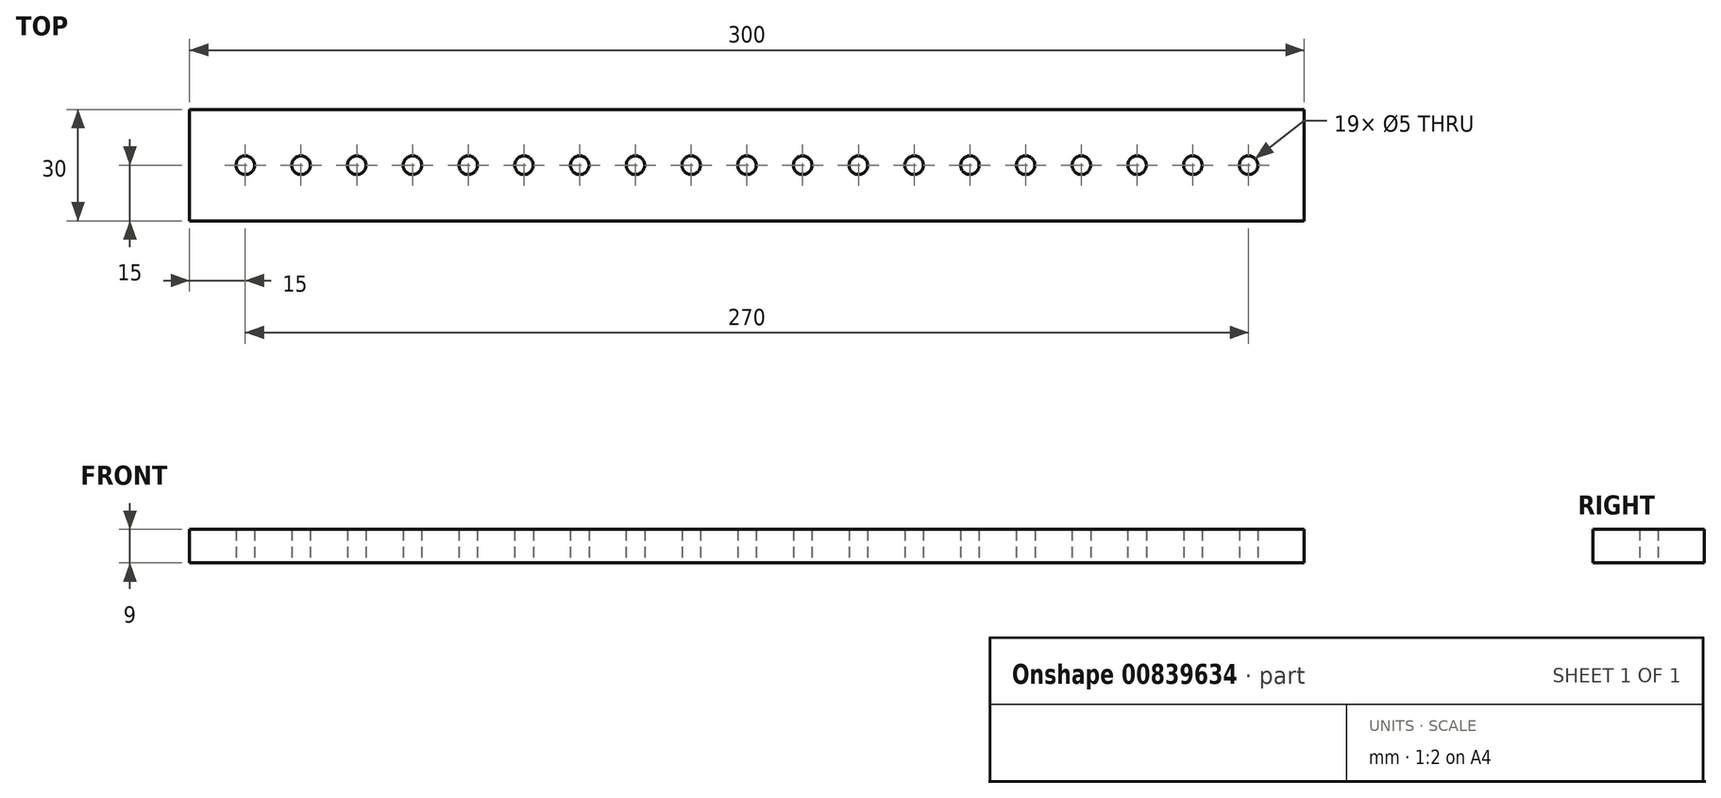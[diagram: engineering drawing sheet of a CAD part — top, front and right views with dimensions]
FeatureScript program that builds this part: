
annotation { "Feature Type Name" : "Feature", "Feature Type Description" : "" }
export const myFeature = defineFeature(function(context is Context, id is Id, definition is map)
    precondition{}
    {
        {
            var Q0;
            Q0=qCreatedBy(makeId("Top.planeOp"),FACE);
            var sketch = newSketch(context, id + "F0", { "sketchPlane" : qUnion([Q0])});
            skLineSegment(sketch, "E0.bottom", {"start": v(150, -15) * mm, "end": v(-150, -15) * mm});
            skLineSegment(sketch, "E0.top", {"start": v(150, 15) * mm, "end": v(-150, 15) * mm});
            skLineSegment(sketch, "E0.left", {"start": v(150, -15) * mm, "end": v(150, 15) * mm});
            skLineSegment(sketch, "E0.right", {"start": v(-150, -15) * mm, "end": v(-150, 15) * mm});
            skPoint(sketch, "E0.middle", {"position": v(0, 0) * mm});
            skCircle(sketch, "E1", {"center": v(-135, 0) * mm, "radius": 2.5 * mm});
            skCircle(sketch, "E2.1.0.0", {"center": v(-120, 0) * mm, "radius": 2.5 * mm});
            skCircle(sketch, "E2.2.0.0", {"center": v(-105, 0) * mm, "radius": 2.5 * mm});
            skCircle(sketch, "E2.3.0.0", {"center": v(-90, 0) * mm, "radius": 2.5 * mm});
            skCircle(sketch, "E2.4.0.0", {"center": v(-75, 0) * mm, "radius": 2.5 * mm});
            skCircle(sketch, "E2.5.0.0", {"center": v(-60, 0) * mm, "radius": 2.5 * mm});
            skCircle(sketch, "E2.6.0.0", {"center": v(-45, 0) * mm, "radius": 2.5 * mm});
            skCircle(sketch, "E2.7.0.0", {"center": v(-30, 0) * mm, "radius": 2.5 * mm});
            skCircle(sketch, "E2.8.0.0", {"center": v(-15, 0) * mm, "radius": 2.5 * mm});
            skCircle(sketch, "E2.9.0.0", {"center": v(0, 0) * mm, "radius": 2.5 * mm});
            skCircle(sketch, "E2.10.0.0", {"center": v(15, 0) * mm, "radius": 2.5 * mm});
            skCircle(sketch, "E2.11.0.0", {"center": v(30, 0) * mm, "radius": 2.5 * mm});
            skCircle(sketch, "E2.12.0.0", {"center": v(45, 0) * mm, "radius": 2.5 * mm});
            skCircle(sketch, "E2.13.0.0", {"center": v(60, 0) * mm, "radius": 2.5 * mm});
            skCircle(sketch, "E2.14.0.0", {"center": v(75, 0) * mm, "radius": 2.5 * mm});
            skCircle(sketch, "E2.15.0.0", {"center": v(90, 0) * mm, "radius": 2.5 * mm});
            skCircle(sketch, "E2.16.0.0", {"center": v(105, 0) * mm, "radius": 2.5 * mm});
            skCircle(sketch, "E2.17.0.0", {"center": v(120, 0) * mm, "radius": 2.5 * mm});
            skCircle(sketch, "E2.18.0.0", {"center": v(135, 0) * mm, "radius": 2.5 * mm});
            skLineSegment(sketch, "E2.direction1", {"start": v(-135, 0) * mm, "end": v(-120, 0) * mm, "construction": true});
            skSolve(sketch);
        }
        {
            var Q0;
            Q0=makeQuery(id+"F0.imprint","IMPRINT",FACE,{"disambiguationData":[TD([[makeQuery(id+"F0.imprint","IMPRINT",EDGE,{"derivedFrom":sQuery(id+"F0.wireOp",EDGE,"E0.bottom")}),-1.0]])]});
            extrude(context, id + "F1", {"entities" : qUnion([Q0]), "depth" : 9 * mm, "offsetDistance" : 25 * mm});
        }
    });
